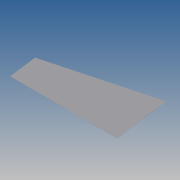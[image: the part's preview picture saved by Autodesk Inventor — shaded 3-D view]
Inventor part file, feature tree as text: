
AUTODESK INVENTOR PART (.ipt)
format: ipt  version: 2014 SP1 (Build 180222100, 222)  size: 72,704 bytes
history: native  units: in
note: dims shown in document units (in); Inventor stores cm internally (conversion verified against a paired STEP export)
features: extrude x1, sketch x1
ambient origin geometry x8: Origin, YZ Plane, XZ Plane, XY Plane, X Axis, Y Axis, Z Axis, Center Point
bodies: Solid1 (feature_tree)
feature tree (2):
  extrude  "Extrusion1"  Depth=0.0394in
  sketch  "Sketch1"  dims[d0=169.2913in d1=169.2913in d2=165.0deg d5=1.9685in d7=1.9685in d8=89.7638in d9=0.0394in d10=0.0in]
